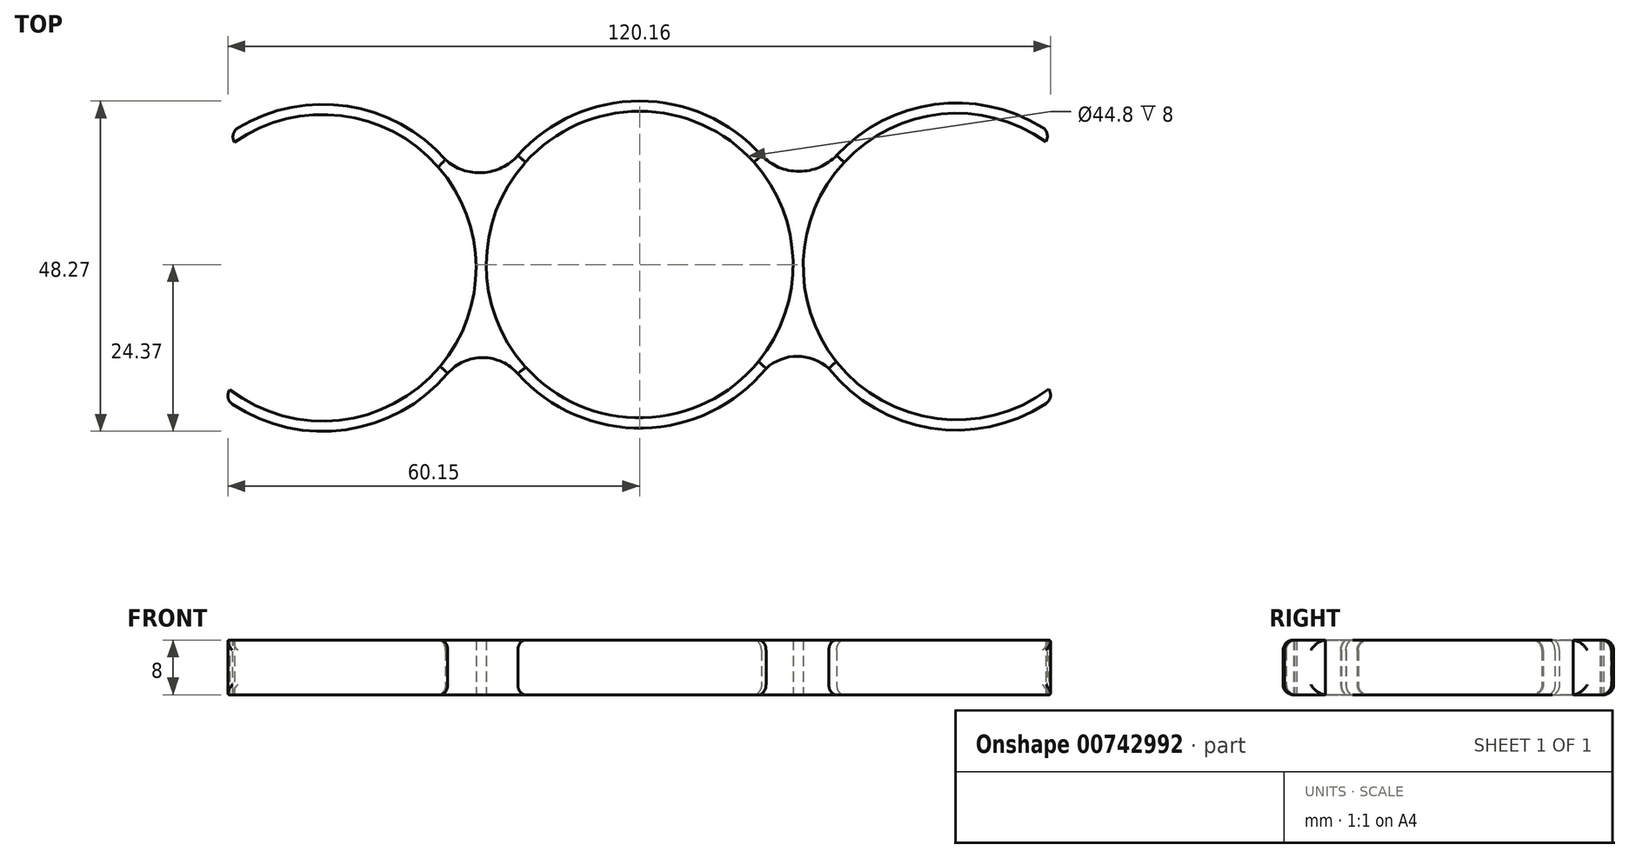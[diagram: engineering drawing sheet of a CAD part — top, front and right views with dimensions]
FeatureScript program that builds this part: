
annotation { "Feature Type Name" : "Feature", "Feature Type Description" : "" }
export const myFeature = defineFeature(function(context is Context, id is Id, definition is map)
    precondition{}
    {
        {
            var Q0;
            Q0=qCreatedBy(makeId("Top.planeOp"),FACE);
            var sketch = newSketch(context, id + "F0", { "sketchPlane" : qUnion([Q0])});
            skCircle(sketch, "E0", {"center": v(0, 0) * mm, "radius": 22.4 * mm});
            skCircle(sketch, "E1", {"center": v(0, 0) * mm, "radius": 23.9 * mm});
            skCircle(sketch, "E2", {"center": v(-46.3, -0.47) * mm, "radius": 23.9 * mm});
            skPoint(sketch, "E2.first.point", {"position": v(-22.4, 0) * mm});
            skPoint(sketch, "E2.second.point", {"position": v(-70.2, 0) * mm});
            skPoint(sketch, "E2.third.point", {"position": v(-46.03, -24.37) * mm});
            skCircle(sketch, "E3", {"center": v(46.3, -0.29) * mm, "radius": 23.9 * mm});
            skPoint(sketch, "E3.first.point", {"position": v(22.4, 0) * mm});
            skPoint(sketch, "E3.second.point", {"position": v(70.2, 0) * mm});
            skPoint(sketch, "E3.third.point", {"position": v(45.79, -24.18) * mm});
            skCircle(sketch, "E4", {"center": v(-46.3, -0.47) * mm, "radius": 22.4 * mm});
            skCircle(sketch, "E5", {"center": v(46.3, -0.29) * mm, "radius": 22.4 * mm});
            skArc(sketch, "E6", {"start": v(-28.36, 15.32) * mm, "mid": v(-22.94, 13.43) * mm, "end": v(-17.79, 15.96) * mm});
            skArc(sketch, "E7", {"start": v(17.79, 15.96) * mm, "mid": v(23.28, 13.62) * mm, "end": v(28.77, 15.96) * mm});
            skArc(sketch, "E8", {"start": v(-17.79, -15.96) * mm, "mid": v(-22.89, -13.6) * mm, "end": v(-28.02, -15.88) * mm});
            skArc(sketch, "E9", {"start": v(27.62, -15.2) * mm, "mid": v(23.04, -13.4) * mm, "end": v(18.46, -15.18) * mm});
            skArc(sketch, "E10", {"start": v(-70.2, 21) * mm, "mid": v(-49.2, 0) * mm, "end": v(-70.2, -21) * mm});
            skArc(sketch, "E11", {"start": v(70.2, 21) * mm, "mid": v(49.22, 1.04) * mm, "end": v(68.11, -20.9) * mm});
            skSolve(sketch);
        }
        {
            var Q0;
            {var subQ0=sQuery(id+"F0.wireOp",EDGE,"E2");var subQ4=sQuery(id+"F0.wireOp",EDGE,"E1");var subQ7=makeQuery(id+"F0.imprint","INTERSECT",VERTEX,{"disambiguationData":[OD(0.0)],"derivedFrom":[subQ4,subQ0]});Q0=makeQuery(id+"F0.imprint","IMPRINT",FACE,{"disambiguationData":[TD([[makeQuery(id+"F0.imprint","IMPRINT",EDGE,{"disambiguationData":[TD([[subQ7,-1.0]])],"derivedFrom":subQ4}),-1.0]])]});}
            var Q1;
            {var subQ0=sQuery(id+"F0.wireOp",EDGE,"E8");var subQ1=sQuery(id+"F0.wireOp",EDGE,"E1");var subQ2=makeQuery(id+"F0.imprint","INTERSECT",VERTEX,{"disambiguationData":[OD(1.0)],"derivedFrom":[subQ1,subQ0]});Q1=makeQuery(id+"F0.imprint","IMPRINT",FACE,{"disambiguationData":[TD([[makeQuery(id+"F0.imprint","IMPRINT",EDGE,{"disambiguationData":[TD([[subQ2,1.0]])],"derivedFrom":subQ1}),-1.0]])]});}
            var Q2;
            {var subQ6=sQuery(id+"F0.wireOp",EDGE,"E2");var subQ7=sQuery(id+"F0.wireOp",EDGE,"E0");var subQ8=makeQuery(id+"F0.imprint","INTERSECT",VERTEX,{"disambiguationData":[OD(1.0)],"derivedFrom":[subQ7,subQ6]});Q2=makeQuery(id+"F0.imprint","IMPRINT",FACE,{"disambiguationData":[TD([[makeQuery(id+"F0.imprint","IMPRINT",EDGE,{"disambiguationData":[TD([[subQ8,-1.0]])],"derivedFrom":subQ7}),-1.0]])]});}
            var Q3;
            {var subQ0=sQuery(id+"F0.wireOp",EDGE,"E9");Q3=makeQuery(id+"F0.imprint","IMPRINT",FACE,{"disambiguationData":[TD([[makeQuery(id+"F0.imprint","IMPRINT",EDGE,{"derivedFrom":subQ0}),-1.0]])]});}
            var Q4;
            {var subQ0=sQuery(id+"F0.wireOp",EDGE,"E3");var subQ2=sQuery(id+"F0.wireOp",EDGE,"E1");var subQ3=makeQuery(id+"F0.imprint","INTERSECT",VERTEX,{"disambiguationData":[OD(1.0)],"derivedFrom":[subQ2,subQ0]});Q4=makeQuery(id+"F0.imprint","IMPRINT",FACE,{"disambiguationData":[TD([[makeQuery(id+"F0.imprint","IMPRINT",EDGE,{"disambiguationData":[TD([[subQ3,-1.0]])],"derivedFrom":subQ2}),-1.0]])]});}
            var Q5;
            {var subQ0=sQuery(id+"F0.wireOp",EDGE,"E6");var subQ1=sQuery(id+"F0.wireOp",EDGE,"E1");var subQ2=makeQuery(id+"F0.imprint","INTERSECT",VERTEX,{"disambiguationData":[OD(1.0)],"derivedFrom":[subQ1,subQ0]});Q5=makeQuery(id+"F0.imprint","IMPRINT",FACE,{"disambiguationData":[TD([[makeQuery(id+"F0.imprint","IMPRINT",EDGE,{"disambiguationData":[TD([[subQ2,-1.0]])],"derivedFrom":subQ1}),-1.0]])]});}
            var Q6;
            {var subQ3=sQuery(id+"F0.wireOp",EDGE,"E2");var subQ9=sQuery(id+"F0.wireOp",EDGE,"E0");var subQ10=makeQuery(id+"F0.imprint","INTERSECT",VERTEX,{"disambiguationData":[OD(0.0)],"derivedFrom":[subQ9,subQ3]});Q6=makeQuery(id+"F0.imprint","IMPRINT",FACE,{"disambiguationData":[TD([[makeQuery(id+"F0.imprint","IMPRINT",EDGE,{"disambiguationData":[TD([[subQ10,1.0]])],"derivedFrom":subQ9}),-1.0]])]});}
            var Q7;
            {var subQ0=sQuery(id+"F0.wireOp",EDGE,"E2");var subQ1=sQuery(id+"F0.wireOp",EDGE,"E0");var subQ2=makeQuery(id+"F0.imprint","INTERSECT",VERTEX,{"disambiguationData":[OD(0.0)],"derivedFrom":[subQ1,subQ0]});Q7=makeQuery(id+"F0.imprint","IMPRINT",FACE,{"disambiguationData":[TD([[makeQuery(id+"F0.imprint","IMPRINT",EDGE,{"disambiguationData":[TD([[subQ2,-1.0]])],"derivedFrom":subQ1}),-1.0]])]});}
            var Q8;
            {var subQ0=sQuery(id+"F0.wireOp",EDGE,"E3");var subQ5=sQuery(id+"F0.wireOp",EDGE,"E0");var subQ6=makeQuery(id+"F0.imprint","INTERSECT",VERTEX,{"disambiguationData":[OD(0.0)],"derivedFrom":[subQ5,subQ0]});Q8=makeQuery(id+"F0.imprint","IMPRINT",FACE,{"disambiguationData":[TD([[makeQuery(id+"F0.imprint","IMPRINT",EDGE,{"disambiguationData":[TD([[subQ6,1.0]])],"derivedFrom":subQ5}),-1.0]])]});}
            var Q9;
            {var subQ0=sQuery(id+"F0.wireOp",EDGE,"E7");Q9=makeQuery(id+"F0.imprint","IMPRINT",FACE,{"disambiguationData":[TD([[makeQuery(id+"F0.imprint","IMPRINT",EDGE,{"derivedFrom":subQ0}),-1.0]])]});}
            var Q10;
            {var subQ0=sQuery(id+"F0.wireOp",EDGE,"E4");var subQ1=sQuery(id+"F0.wireOp",EDGE,"E1");var subQ2=makeQuery(id+"F0.imprint","INTERSECT",VERTEX,{"disambiguationData":[OD(1.0)],"derivedFrom":[subQ1,subQ0]});Q10=makeQuery(id+"F0.imprint","IMPRINT",FACE,{"disambiguationData":[TD([[makeQuery(id+"F0.imprint","IMPRINT",EDGE,{"disambiguationData":[TD([[subQ2,-1.0]])],"derivedFrom":subQ1}),-1.0]])]});}
            var Q11;
            {var subQ1=sQuery(id+"F0.wireOp",EDGE,"E1");var subQ5=sQuery(id+"F0.wireOp",EDGE,"E3");var subQ7=makeQuery(id+"F0.imprint","INTERSECT",VERTEX,{"disambiguationData":[OD(0.0)],"derivedFrom":[subQ1,subQ5]});Q11=makeQuery(id+"F0.imprint","IMPRINT",FACE,{"disambiguationData":[TD([[makeQuery(id+"F0.imprint","IMPRINT",EDGE,{"disambiguationData":[TD([[subQ7,1.0]])],"derivedFrom":subQ1}),-1.0]])]});}
            extrude(context, id + "F1", {"entities" : qUnion([Q0, Q1, Q2, Q3, Q4, Q5, Q6, Q7, Q8, Q9, Q10, Q11]), "depth" : 8 * mm, "offsetDistance" : 25 * mm});
        }
        {
            var Q0;
            {var subQ0=sQuery(id+"F0.wireOp",EDGE,"E2");Q0=makeQuery(id+"F1.opExtrude","CAP_EDGE",EDGE,{"disambiguationData":[OSD([subQ0]),TDD([makeQuery(id+"F0.imprint","IMPRINT",EDGE,{"disambiguationData":[TD([[makeQuery(id+"F0.imprint","INTERSECT",VERTEX,{"derivedFrom":[subQ0,sQuery(id+"F0.wireOp",EDGE,"E8")]}),1.0]])],"derivedFrom":subQ0})])],"isStart":false});}
            var Q1;
            {var subQ0=sQuery(id+"F0.wireOp",EDGE,"E1");Q1=makeQuery(id+"F1.opExtrude","CAP_EDGE",EDGE,{"disambiguationData":[OSD([subQ0]),TDD([makeQuery(id+"F0.imprint","IMPRINT",EDGE,{"disambiguationData":[TD([[makeQuery(id+"F0.imprint","INTERSECT",VERTEX,{"disambiguationData":[OD(0.0)],"derivedFrom":[subQ0,sQuery(id+"F0.wireOp",EDGE,"E8")]}),-1.0]])],"derivedFrom":subQ0})])],"isStart":false});}
            var Q2;
            Q2=makeQuery(id+"F1.opExtrude","CAP_EDGE",EDGE,{"disambiguationData":[OSD([sQuery(id+"F0.wireOp",EDGE,"E9")])],"isStart":false});
            var Q3;
            {var subQ0=sQuery(id+"F0.wireOp",EDGE,"E3");Q3=makeQuery(id+"F1.opExtrude","CAP_EDGE",EDGE,{"disambiguationData":[OSD([subQ0]),TDD([makeQuery(id+"F0.imprint","IMPRINT",EDGE,{"disambiguationData":[TD([[makeQuery(id+"F0.imprint","INTERSECT",VERTEX,{"derivedFrom":[subQ0,sQuery(id+"F0.wireOp",EDGE,"E9")]}),-1.0]])],"derivedFrom":subQ0})])],"isStart":false});}
            var Q4;
            Q4=makeQuery(id+"F1.opExtrude","CAP_EDGE",EDGE,{"disambiguationData":[OSD([sQuery(id+"F0.wireOp",EDGE,"E9")])],"isStart":true});
            var Q5;
            {var subQ0=sQuery(id+"F0.wireOp",EDGE,"E3");Q5=makeQuery(id+"F1.opExtrude","CAP_EDGE",EDGE,{"disambiguationData":[OSD([subQ0]),TDD([makeQuery(id+"F0.imprint","IMPRINT",EDGE,{"disambiguationData":[TD([[makeQuery(id+"F0.imprint","INTERSECT",VERTEX,{"derivedFrom":[subQ0,sQuery(id+"F0.wireOp",EDGE,"E9")]}),-1.0]])],"derivedFrom":subQ0})])],"isStart":true});}
            var Q6;
            {var subQ0=sQuery(id+"F0.wireOp",EDGE,"E1");Q6=makeQuery(id+"F1.opExtrude","CAP_EDGE",EDGE,{"disambiguationData":[OSD([subQ0]),TDD([makeQuery(id+"F0.imprint","IMPRINT",EDGE,{"disambiguationData":[TD([[makeQuery(id+"F0.imprint","INTERSECT",VERTEX,{"disambiguationData":[OD(0.0)],"derivedFrom":[subQ0,sQuery(id+"F0.wireOp",EDGE,"E8")]}),-1.0]])],"derivedFrom":subQ0})])],"isStart":true});}
            var Q7;
            Q7=makeQuery(id+"F1.opExtrude","CAP_EDGE",EDGE,{"disambiguationData":[OSD([sQuery(id+"F0.wireOp",EDGE,"E8")])],"isStart":true});
            var Q8;
            {var subQ0=sQuery(id+"F0.wireOp",EDGE,"E2");Q8=makeQuery(id+"F1.opExtrude","CAP_EDGE",EDGE,{"disambiguationData":[OSD([subQ0]),TDD([makeQuery(id+"F0.imprint","IMPRINT",EDGE,{"disambiguationData":[TD([[makeQuery(id+"F0.imprint","INTERSECT",VERTEX,{"derivedFrom":[subQ0,sQuery(id+"F0.wireOp",EDGE,"E8")]}),1.0]])],"derivedFrom":subQ0})])],"isStart":true});}
            var Q9;
            Q9=makeQuery(id+"F1.opExtrude","CAP_EDGE",EDGE,{"disambiguationData":[OSD([sQuery(id+"F0.wireOp",EDGE,"E7")])],"isStart":false});
            var Q10;
            {var subQ0=sQuery(id+"F0.wireOp",EDGE,"E1");Q10=makeQuery(id+"F1.opExtrude","CAP_EDGE",EDGE,{"disambiguationData":[OSD([subQ0]),TDD([makeQuery(id+"F0.imprint","IMPRINT",EDGE,{"disambiguationData":[TD([[makeQuery(id+"F0.imprint","INTERSECT",VERTEX,{"disambiguationData":[OD(0.0)],"derivedFrom":[subQ0,sQuery(id+"F0.wireOp",EDGE,"E6")]}),1.0]])],"derivedFrom":subQ0})])],"isStart":false});}
            var Q11;
            {var subQ0=sQuery(id+"F0.wireOp",EDGE,"E3");Q11=makeQuery(id+"F1.opExtrude","CAP_EDGE",EDGE,{"disambiguationData":[OSD([subQ0]),TDD([makeQuery(id+"F0.imprint","IMPRINT",EDGE,{"disambiguationData":[TD([[makeQuery(id+"F0.imprint","INTERSECT",VERTEX,{"derivedFrom":[subQ0,sQuery(id+"F0.wireOp",EDGE,"E7")]}),1.0]])],"derivedFrom":subQ0})])],"isStart":false});}
            var Q12;
            {var subQ0=sQuery(id+"F0.wireOp",EDGE,"E3");Q12=makeQuery(id+"F1.opExtrude","CAP_EDGE",EDGE,{"disambiguationData":[OSD([subQ0]),TDD([makeQuery(id+"F0.imprint","IMPRINT",EDGE,{"disambiguationData":[TD([[makeQuery(id+"F0.imprint","INTERSECT",VERTEX,{"derivedFrom":[subQ0,sQuery(id+"F0.wireOp",EDGE,"E7")]}),1.0]])],"derivedFrom":subQ0})])],"isStart":true});}
            var Q13;
            Q13=makeQuery(id+"F1.opExtrude","CAP_EDGE",EDGE,{"disambiguationData":[OSD([sQuery(id+"F0.wireOp",EDGE,"E6")])],"isStart":false});
            var Q14;
            {var subQ0=sQuery(id+"F0.wireOp",EDGE,"E2");Q14=makeQuery(id+"F1.opExtrude","CAP_EDGE",EDGE,{"disambiguationData":[OSD([subQ0]),TDD([makeQuery(id+"F0.imprint","IMPRINT",EDGE,{"disambiguationData":[TD([[makeQuery(id+"F0.imprint","INTERSECT",VERTEX,{"derivedFrom":[subQ0,sQuery(id+"F0.wireOp",EDGE,"E6")]}),-1.0]])],"derivedFrom":subQ0})])],"isStart":false});}
            var Q15;
            {var subQ0=sQuery(id+"F0.wireOp",EDGE,"E2");Q15=makeQuery(id+"F1.opExtrude","CAP_EDGE",EDGE,{"disambiguationData":[OSD([subQ0]),TDD([makeQuery(id+"F0.imprint","IMPRINT",EDGE,{"disambiguationData":[TD([[makeQuery(id+"F0.imprint","INTERSECT",VERTEX,{"derivedFrom":[subQ0,sQuery(id+"F0.wireOp",EDGE,"E6")]}),-1.0]])],"derivedFrom":subQ0})])],"isStart":true});}
            var Q16;
            Q16=makeQuery(id+"F1.opExtrude","CAP_EDGE",EDGE,{"disambiguationData":[OSD([sQuery(id+"F0.wireOp",EDGE,"E6")])],"isStart":true});
            var Q17;
            {var subQ0=sQuery(id+"F0.wireOp",EDGE,"E1");Q17=makeQuery(id+"F1.opExtrude","CAP_EDGE",EDGE,{"disambiguationData":[OSD([subQ0]),TDD([makeQuery(id+"F0.imprint","IMPRINT",EDGE,{"disambiguationData":[TD([[makeQuery(id+"F0.imprint","INTERSECT",VERTEX,{"disambiguationData":[OD(0.0)],"derivedFrom":[subQ0,sQuery(id+"F0.wireOp",EDGE,"E6")]}),1.0]])],"derivedFrom":subQ0})])],"isStart":true});}
            var Q18;
            Q18=makeQuery(id+"F1.opExtrude","CAP_EDGE",EDGE,{"disambiguationData":[OSD([sQuery(id+"F0.wireOp",EDGE,"E7")])],"isStart":true});
            var Q19;
            {var subQ0=sQuery(id+"F0.wireOp",EDGE,"E11");var subQ1=sQuery(id+"F0.wireOp",EDGE,"E3");Q19=makeQuery(id+"F1.opExtrude","SWEPT_EDGE",EDGE,{"disambiguationData":[OSD([subQ1,subQ0]),TDD([makeQuery(id+"F0.imprint","INTERSECT",VERTEX,{"disambiguationData":[OD(1.0)],"derivedFrom":[subQ1,subQ0]})])]});}
            var Q20;
            {var subQ0=sQuery(id+"F0.wireOp",EDGE,"E11");var subQ1=sQuery(id+"F0.wireOp",EDGE,"E3");Q20=makeQuery(id+"F1.opExtrude","SWEPT_EDGE",EDGE,{"disambiguationData":[OSD([subQ1,subQ0]),TDD([makeQuery(id+"F0.imprint","INTERSECT",VERTEX,{"disambiguationData":[OD(0.0)],"derivedFrom":[subQ1,subQ0]})])]});}
            var Q21;
            {var subQ0=sQuery(id+"F0.wireOp",EDGE,"E10");var subQ1=sQuery(id+"F0.wireOp",EDGE,"E2");Q21=makeQuery(id+"F1.opExtrude","SWEPT_EDGE",EDGE,{"disambiguationData":[OSD([subQ1,subQ0]),TDD([makeQuery(id+"F0.imprint","INTERSECT",VERTEX,{"disambiguationData":[OD(0.0)],"derivedFrom":[subQ1,subQ0]})])]});}
            var Q22;
            {var subQ0=sQuery(id+"F0.wireOp",EDGE,"E10");var subQ1=sQuery(id+"F0.wireOp",EDGE,"E2");Q22=makeQuery(id+"F1.opExtrude","SWEPT_EDGE",EDGE,{"disambiguationData":[OSD([subQ1,subQ0]),TDD([makeQuery(id+"F0.imprint","INTERSECT",VERTEX,{"disambiguationData":[OD(1.0)],"derivedFrom":[subQ1,subQ0]})])]});}
            fillet(context, id + "F2", {"entities" : qUnion([Q0, Q1, Q2, Q3, Q4, Q5, Q6, Q7, Q8, Q9, Q10, Q11, Q12, Q13, Q14, Q15, Q16, Q17, Q18, Q19, Q20, Q21, Q22]), "radius" : 1.5 * mm, "tangentPropagation" : true, "allowEdgeOverflow" : false});
        }
    });
